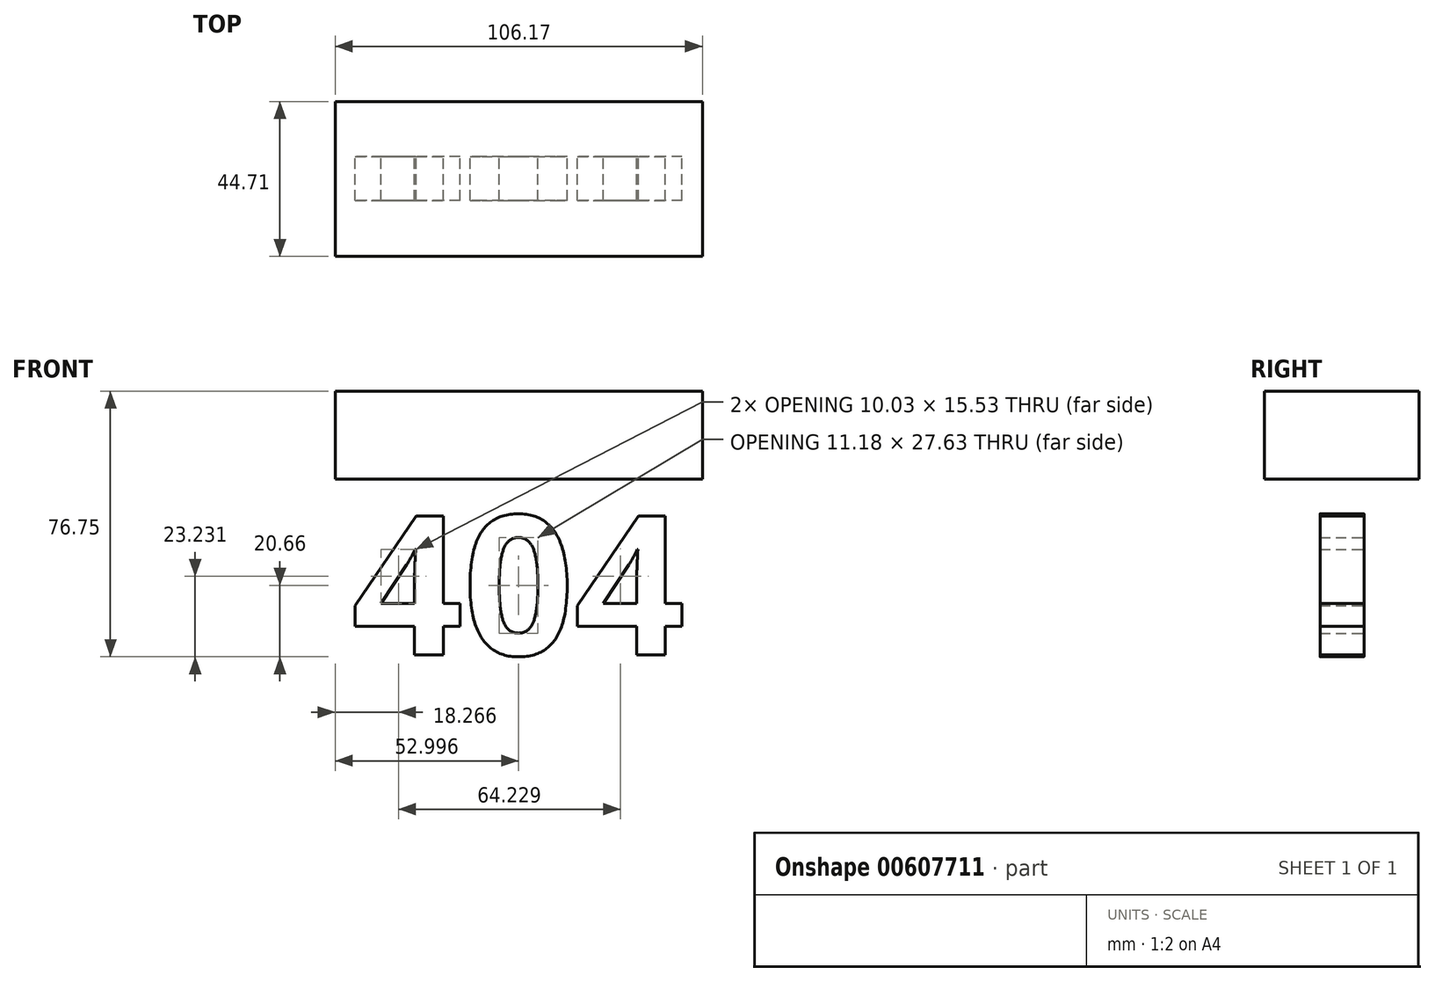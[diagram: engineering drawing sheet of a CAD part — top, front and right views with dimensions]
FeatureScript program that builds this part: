
annotation { "Feature Type Name" : "Feature", "Feature Type Description" : "" }
export const myFeature = defineFeature(function(context is Context, id is Id, definition is map)
    precondition{}
    {
        {
            var Q0;
            Q0=qCreatedBy(makeId("Front.planeOp"),FACE);
            var sketch = newSketch(context, id + "F0", { "sketchPlane" : qUnion([Q0])});
            skText(sketch, "E0", { "text": "404", "fontName": "OpenSans-Bold.ttf"});
            const initialGuessF0  = {"E0": [-0.06363, 0, 1, 0, 0.04051]};
            skSetInitialGuess(sketch, initialGuessF0);
            skSolve(sketch);
        }
        {
            var Q0;
            Q0=makeQuery(id+"F0.imprint","IMPRINT",FACE,{"disambiguationData":[TD([[makeQuery(id+"F0.imprint","IMPRINT",EDGE,{"derivedFrom":sQuery(id+"F0.wireOp",EDGE,"E0.sketch_text.stroke-0")}),-1.0]])]});
            var Q1;
            Q1=makeQuery(id+"F0.imprint","IMPRINT",FACE,{"disambiguationData":[TD([[makeQuery(id+"F0.imprint","IMPRINT",EDGE,{"derivedFrom":sQuery(id+"F0.wireOp",EDGE,"E0.sketch_text.stroke-18")}),-1.0]])]});
            var Q2;
            Q2=makeQuery(id+"F0.imprint","IMPRINT",FACE,{"disambiguationData":[TD([[makeQuery(id+"F0.imprint","IMPRINT",EDGE,{"derivedFrom":sQuery(id+"F0.wireOp",EDGE,"E0.sketch_text.stroke-34")}),-1.0]])]});
            extrude(context, id + "F1", {"entities" : qUnion([Q0, Q1, Q2]), "depth" : 12.7 * mm, "offsetDistance" : 25.4 * mm});
        }
        {
            var Q0;
            Q0=qCreatedBy(makeId("Top.planeOp"),FACE);
            var sketch = newSketch(context, id + "F2", { "sketchPlane" : qUnion([Q0])});
            skLineSegment(sketch, "E1.bottom", {"start": v(-68.45, -28.83) * mm, "end": v(37.72, -28.83) * mm});
            skLineSegment(sketch, "E1.top", {"start": v(-68.45, 15.88) * mm, "end": v(37.72, 15.88) * mm});
            skLineSegment(sketch, "E1.left", {"start": v(-68.45, -28.83) * mm, "end": v(-68.45, 15.88) * mm});
            skLineSegment(sketch, "E1.right", {"start": v(37.72, -28.83) * mm, "end": v(37.72, 15.88) * mm});
            skSolve(sketch);
        }
        {
            var Q0;
            Q0 = qSketchRegion(id + "F2", true);
            extrude(context, id + "F3", {"entities" : qUnion([Q0]), "depth" : 25.4 * mm, "offsetDistance" : 25.4 * mm});
        }
        {
            var Q0;
            Q0=makeQuery(id+"F3.opExtrude","SWEPT_BODY",BODY,{"disambiguationData":[OSD([sQuery(id+"F2.wireOp",EDGE,"E1.bottom"),sQuery(id+"F2.wireOp",EDGE,"E1.top"),sQuery(id+"F2.wireOp",EDGE,"E1.left"),sQuery(id+"F2.wireOp",EDGE,"E1.right")])]});
            var Q1;
            Q1=makeQuery(id+"F3.opExtrude","SWEPT_EDGE",EDGE,{"disambiguationData":[OSD([sQuery(id+"F2.wireOp",EDGE,"E1.bottom"),sQuery(id+"F2.wireOp",EDGE,"E1.right")])]});
            var Q2;
            Q2=makeQuery(id+"F3.opExtrude","SWEPT_EDGE",EDGE,{"disambiguationData":[OSD([sQuery(id+"F2.wireOp",EDGE,"E1.bottom"),sQuery(id+"F2.wireOp",EDGE,"E1.left")])]});
            transform(context, id + "F4", {"entities" : qUnion([Q0]), "transformType" : TransformType.TRANSLATION_DISTANCE, "transformDirection" : qUnion([Q2]), "distance" : 50.8 * mm, "oppositeDirection" : true, "makeCopy" : false});
        }
    });
